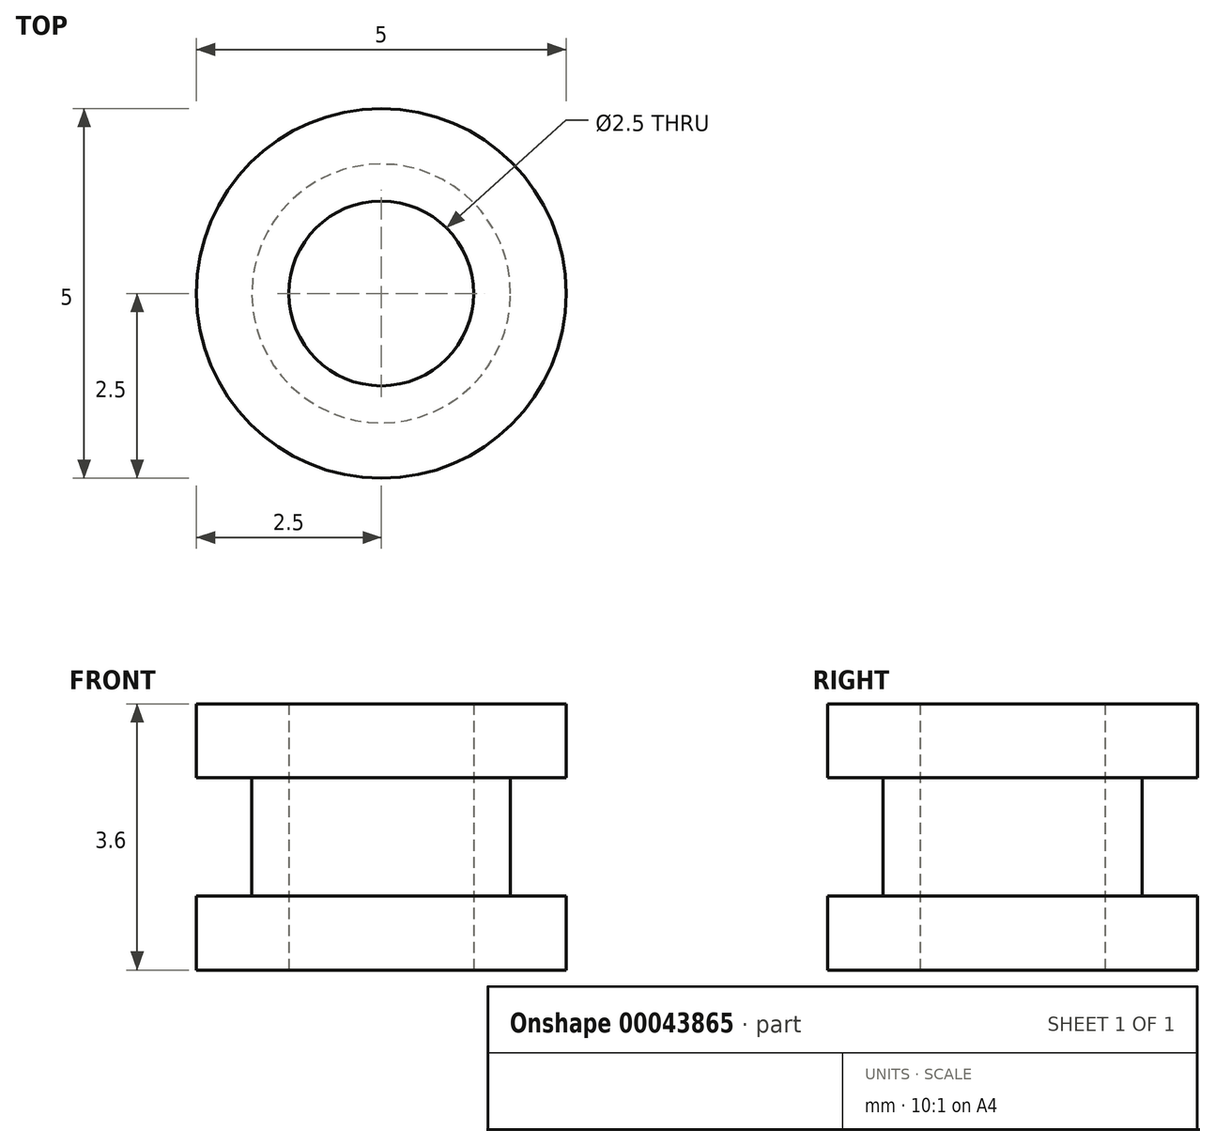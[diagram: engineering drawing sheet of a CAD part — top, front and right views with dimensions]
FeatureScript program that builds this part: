
annotation { "Feature Type Name" : "Feature", "Feature Type Description" : "" }
export const myFeature = defineFeature(function(context is Context, id is Id, definition is map)
    precondition{}
    {
        {
            var Q0;
            Q0=qCreatedBy(makeId("Top.planeOp"),FACE);
            var sketch = newSketch(context, id + "F0", { "sketchPlane" : qUnion([Q0])});
            skCircle(sketch, "E0", {"center": v(0, 0) * mm, "radius": 1.25 * mm});
            skCircle(sketch, "E1", {"center": v(0, 0) * mm, "radius": 2.5 * mm});
            skCircle(sketch, "E2", {"center": v(0, 0) * mm, "radius": 1.75 * mm});
            skSolve(sketch);
        }
        {
            var Q0;
            Q0=makeQuery(id+"F0.imprint","IMPRINT",FACE,{"disambiguationData":[TD([[makeQuery(id+"F0.imprint","IMPRINT",EDGE,{"derivedFrom":sQuery(id+"F0.wireOp",EDGE,"E1")}),1.0]])]});
            var Q1;
            Q1=makeQuery(id+"F0.imprint","IMPRINT",FACE,{"disambiguationData":[TD([[makeQuery(id+"F0.imprint","IMPRINT",EDGE,{"derivedFrom":sQuery(id+"F0.wireOp",EDGE,"E0")}),-1.0]])]});
            extrude(context, id + "F1", {"entities" : qUnion([Q0, Q1]), "depth" : 1 * mm, "offsetDistance" : 25 * mm});
        }
        {
            var Q0;
            Q0=makeQuery(id+"F0.imprint","IMPRINT",FACE,{"disambiguationData":[TD([[makeQuery(id+"F0.imprint","IMPRINT",EDGE,{"derivedFrom":sQuery(id+"F0.wireOp",EDGE,"E0")}),-1.0]])]});
            extrude(context, id + "F2", {"entities" : qUnion([Q0]), "operationType" : NewBodyOperationType.ADD, "oppositeDirection" : true, "depth" : .8 * mm, "offsetDistance" : 25 * mm});
        }
        {
            var Q0;
            Q0=makeQuery(id+"F1.opExtrude","SWEPT_BODY",BODY,{"disambiguationData":[OSD([sQuery(id+"F0.wireOp",EDGE,"E0"),sQuery(id+"F0.wireOp",EDGE,"E1")])]});
            var Q1;
            Q1=makeQuery(id+"F2.opExtrude","CAP_FACE",FACE,{"disambiguationData":[OSD([sQuery(id+"F0.wireOp",EDGE,"E0"),sQuery(id+"F0.wireOp",EDGE,"E2")])],"isStart":false});
            mirror(context, id + "F3", {"operationType" : NewBodyOperationType.ADD, "entities" : qUnion([Q0]), "mirrorPlane" : qUnion([Q1])});
        }
    });
